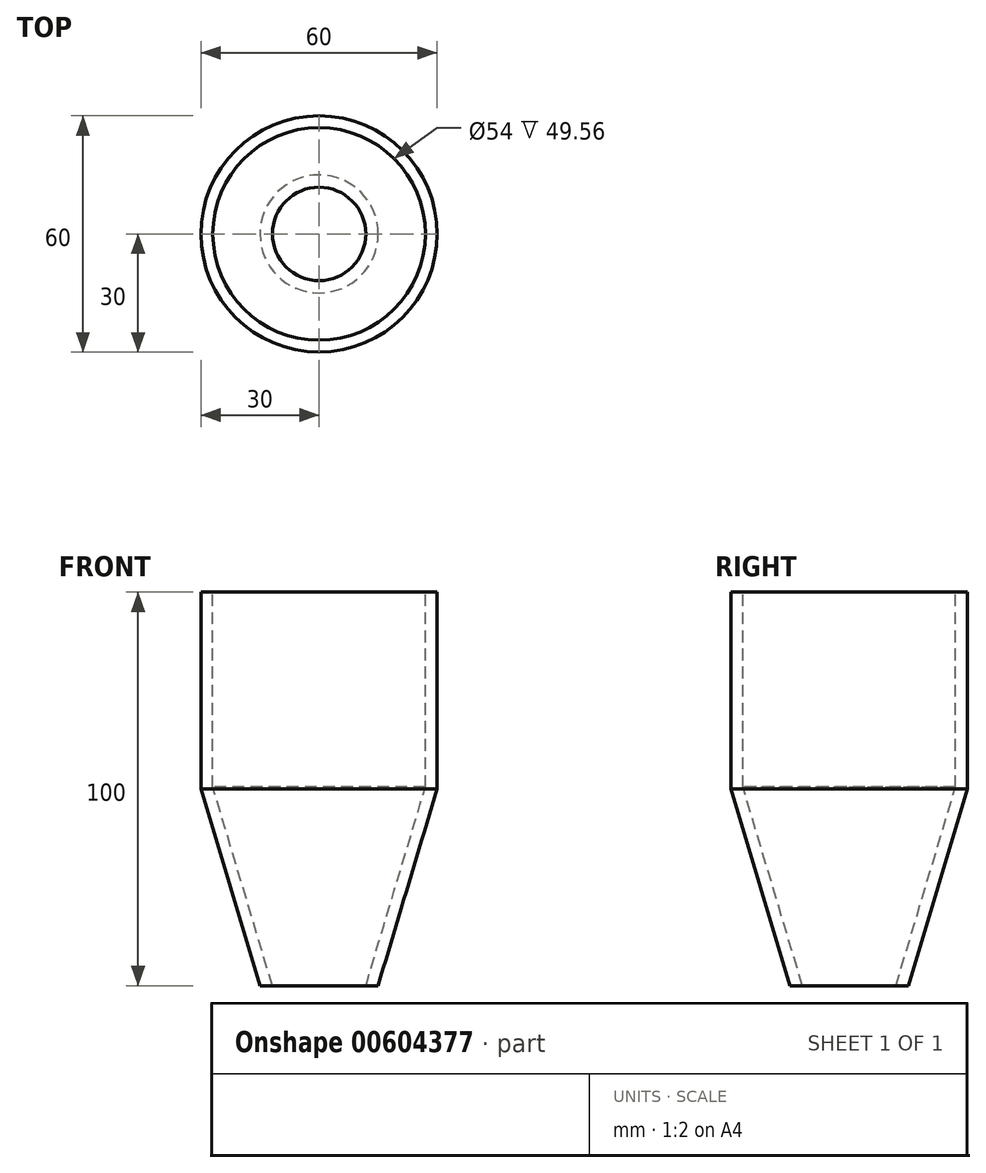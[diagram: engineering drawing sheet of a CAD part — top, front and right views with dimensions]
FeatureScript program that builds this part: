
annotation { "Feature Type Name" : "Feature", "Feature Type Description" : "" }
export const myFeature = defineFeature(function(context is Context, id is Id, definition is map)
    precondition{}
    {
        {
            var Q0;
            Q0=qCreatedBy(makeId("Front.planeOp"),FACE);
            var sketch = newSketch(context, id + "F0", { "sketchPlane" : qUnion([Q0])});
            skLineSegment(sketch, "E0", {"start": v(0, 71.86) * mm, "end": v(0, -67) * mm, "construction": true});
            skLineSegment(sketch, "E1", {"start": v(0, 44.14) * mm, "end": v(30, 44.14) * mm});
            skLineSegment(sketch, "E2", {"start": v(30, 44.14) * mm, "end": v(30, -5.86) * mm});
            skLineSegment(sketch, "E3", {"start": v(30, -5.86) * mm, "end": v(15, -55.86) * mm});
            skLineSegment(sketch, "E4", {"start": v(15, -55.86) * mm, "end": v(0, -55.86) * mm});
            skLineSegment(sketch, "E5", {"start": v(0, 44.14) * mm, "end": v(0, -55.86) * mm});
            skSolve(sketch);
        }
        {
            var Q0;
            Q0 = qSketchRegion(id + "F0", true);
            var Q1;
            Q1=sQuery(id+"F0.wireOp",EDGE,"E0");
            revolve(context, id + "F1", {"entities" : qUnion([Q0]), "axis" : qUnion([Q1]), "revolveType" : RevolveType.FULL});
        }
        {
            var Q0;
            Q0=makeQuery(id+"F1.opRevolve","SWEPT_FACE",FACE,{"disambiguationData":[OSD([sQuery(id+"F0.wireOp",EDGE,"E1")])]});
            var Q1;
            Q1=makeQuery(id+"F1.opRevolve","SWEPT_FACE",FACE,{"disambiguationData":[OSD([sQuery(id+"F0.wireOp",EDGE,"E4")])]});
            shell(context, id + "F2", {"entities" : qUnion([Q0, Q1]), "thickness" : 3 * mm});
        }
    });
